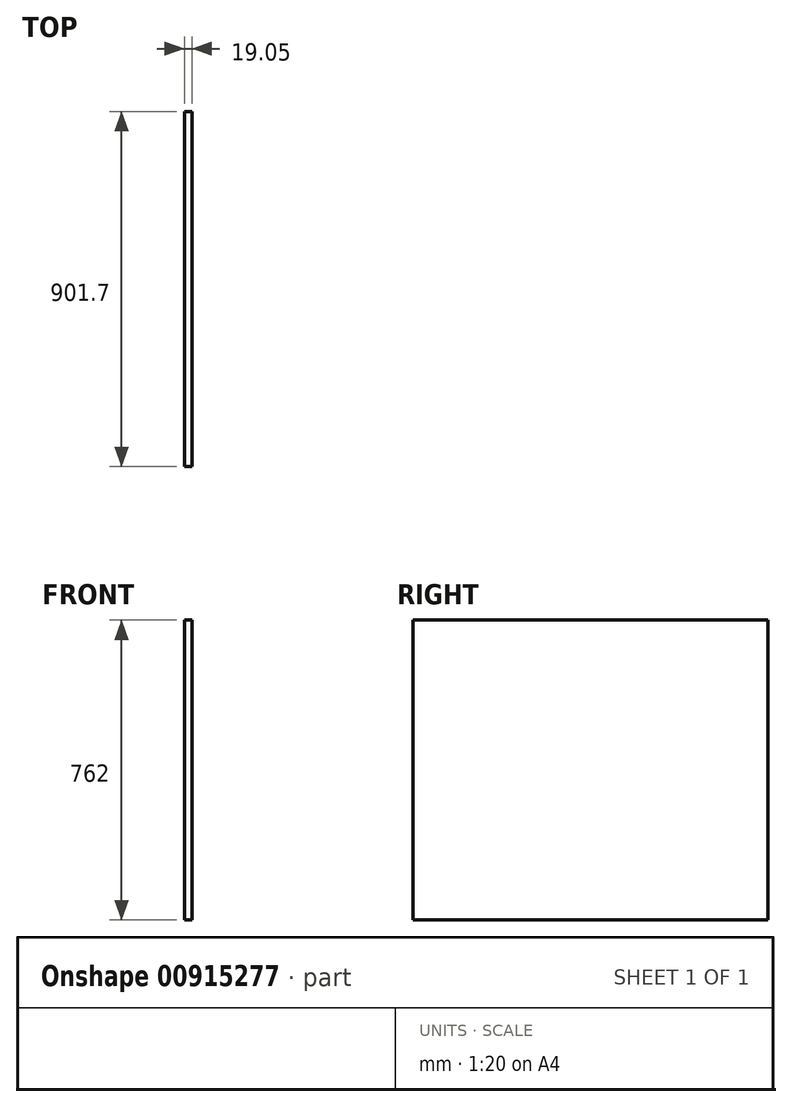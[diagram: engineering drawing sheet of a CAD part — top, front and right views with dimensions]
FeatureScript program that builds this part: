
annotation { "Feature Type Name" : "Feature", "Feature Type Description" : "" }
export const myFeature = defineFeature(function(context is Context, id is Id, definition is map)
    precondition{}
    {
        {
            var Q0;
            Q0=qCreatedBy(makeId("Right.planeOp"),FACE);
            var sketch = newSketch(context, id + "F0", { "sketchPlane" : qUnion([Q0])});
            skLineSegment(sketch, "E0.bottom", {"start": v(450.85, 381) * mm, "end": v(-450.85, 381) * mm});
            skLineSegment(sketch, "E0.top", {"start": v(450.85, -381) * mm, "end": v(-450.85, -381) * mm});
            skLineSegment(sketch, "E0.left", {"start": v(450.85, 381) * mm, "end": v(450.85, -381) * mm});
            skLineSegment(sketch, "E0.right", {"start": v(-450.85, 381) * mm, "end": v(-450.85, -381) * mm});
            skPoint(sketch, "E0.middle", {"position": v(0, 0) * mm});
            skSolve(sketch);
        }
        {
            var Q0;
            Q0=makeQuery(id+"F0.imprint","IMPRINT",FACE,{"disambiguationData":[TD([[makeQuery(id+"F0.imprint","IMPRINT",EDGE,{"derivedFrom":sQuery(id+"F0.wireOp",EDGE,"E0.bottom")}),1.0]])]});
            extrude(context, id + "F1", {"entities" : qUnion([Q0]), "depth" : 19.05 * mm, "offsetDistance" : 25.4 * mm});
        }
    });
